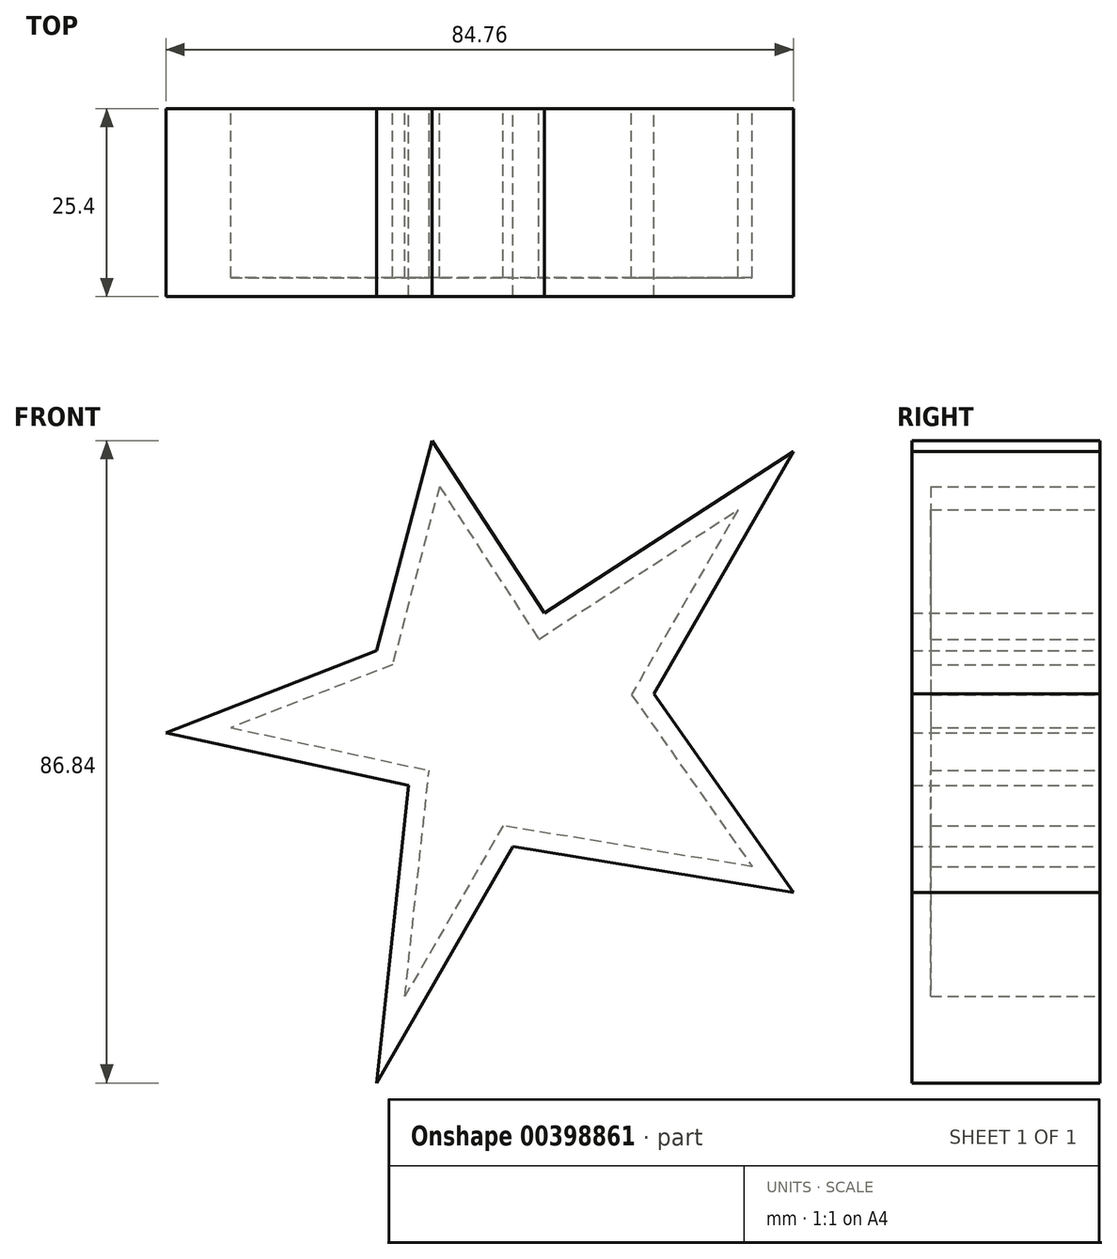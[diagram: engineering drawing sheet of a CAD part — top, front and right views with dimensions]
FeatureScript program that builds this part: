
annotation { "Feature Type Name" : "Feature", "Feature Type Description" : "" }
export const myFeature = defineFeature(function(context is Context, id is Id, definition is map)
    precondition{}
    {
        {
            var Q0;
            Q0=qCreatedBy(makeId("Front.planeOp"),FACE);
            var sketch = newSketch(context, id + "F0", { "sketchPlane" : qUnion([Q0])});
            skLineSegment(sketch, "E0", {"start": v(0, 75.54) * mm, "end": v(0, -76.85) * mm});
            skLineSegment(sketch, "E1", {"start": v(0, 28.4) * mm, "end": v(15.16, 5.08) * mm});
            skLineSegment(sketch, "E2", {"start": v(15.16, 5.08) * mm, "end": v(48.8, 26.95) * mm});
            skLineSegment(sketch, "E3", {"start": v(48.8, 26.95) * mm, "end": v(29.96, -5.8) * mm});
            skLineSegment(sketch, "E4", {"start": v(29.96, -5.8) * mm, "end": v(48.8, -32.68) * mm});
            skLineSegment(sketch, "E5", {"start": v(48.8, -32.68) * mm, "end": v(10.93, -26.45) * mm});
            skLineSegment(sketch, "E6", {"start": v(10.93, -26.45) * mm, "end": v(-7.48, -58.44) * mm});
            skLineSegment(sketch, "E7", {"start": v(-7.48, -58.44) * mm, "end": v(-3.17, -18.19) * mm});
            skLineSegment(sketch, "E8", {"start": v(0, 28.4) * mm, "end": v(-7.48, 0) * mm});
            skLineSegment(sketch, "E9", {"start": v(-7.48, 0) * mm, "end": v(-35.95, -11.08) * mm});
            skLineSegment(sketch, "E10", {"start": v(-35.95, -11.08) * mm, "end": v(-3.17, -18.19) * mm});
            skSolve(sketch);
        }
        {
            var Q0;
            Q0 = qSketchRegion(id + "F0", true);
            extrude(context, id + "F1", {"entities" : qUnion([Q0]), "depth" : 25.4 * mm});
        }
        {
            var Q0;
            Q0=makeQuery(id+"F1.opExtrude","CAP_FACE",FACE,{"disambiguationData":[OSD([sQuery(id+"F0.wireOp",EDGE,"E1"),sQuery(id+"F0.wireOp",EDGE,"E2"),sQuery(id+"F0.wireOp",EDGE,"E3"),sQuery(id+"F0.wireOp",EDGE,"E4"),sQuery(id+"F0.wireOp",EDGE,"E5"),sQuery(id+"F0.wireOp",EDGE,"E6"),sQuery(id+"F0.wireOp",EDGE,"E7"),sQuery(id+"F0.wireOp",EDGE,"E8"),sQuery(id+"F0.wireOp",EDGE,"E9"),sQuery(id+"F0.wireOp",EDGE,"E10")])],"isStart":true});
            shell(context, id + "F2", {"entities" : qUnion([Q0]), "thickness" : 2.54 * mm});
        }
    });
